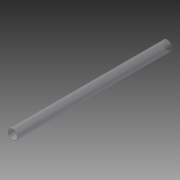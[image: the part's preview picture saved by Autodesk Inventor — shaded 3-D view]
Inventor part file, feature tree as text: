
AUTODESK INVENTOR PART (.ipt)
format: ipt  version: 2014 (Build 180170000, 170)  size: 71,168 bytes
history: native  units: in
note: dims shown in document units (in); Inventor stores cm internally (conversion verified against a paired STEP export)
features: extrude x1, sketch x1
ambient origin geometry x8: Origin, YZ Plane, XZ Plane, XY Plane, X Axis, Y Axis, Z Axis, Center Point
bodies: Solid1 (feature_tree)
feature tree (2):
  extrude  "Extrusion1"  Depth=15.5in
  sketch  "Sketch1"  dims[d0=1.0in d1=0.875in d2=15.5in d3=0.0in]
